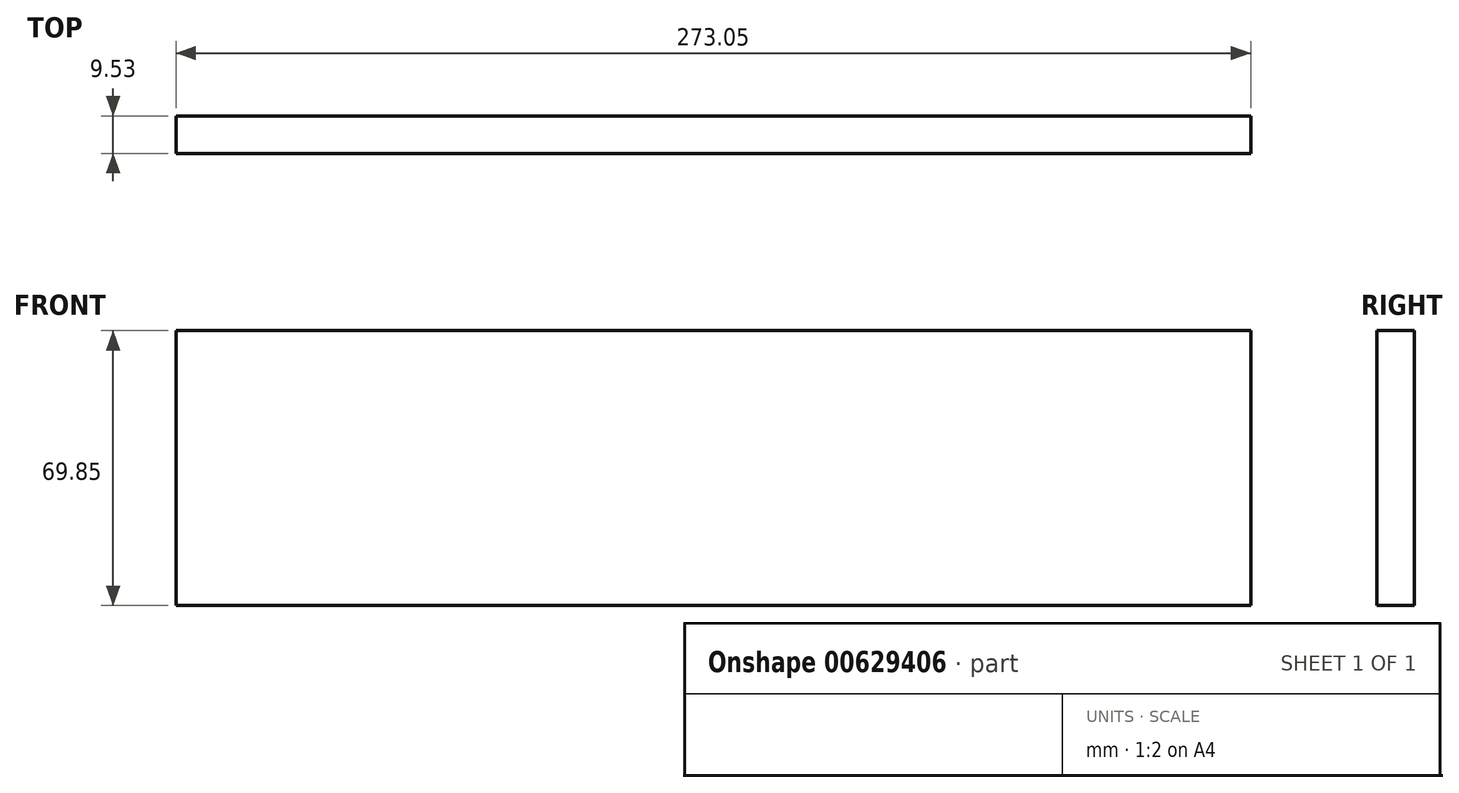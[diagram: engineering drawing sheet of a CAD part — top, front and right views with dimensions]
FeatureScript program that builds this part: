
annotation { "Feature Type Name" : "Feature", "Feature Type Description" : "" }
export const myFeature = defineFeature(function(context is Context, id is Id, definition is map)
    precondition{}
    {
        {
            var Q0;
            Q0=qCreatedBy(makeId("Front.planeOp"),FACE);
            var sketch = newSketch(context, id + "F0", { "sketchPlane" : qUnion([Q0])});
            skLineSegment(sketch, "E0.bottom", {"start": v(0, 0) * mm, "end": v(273.05, 0) * mm});
            skLineSegment(sketch, "E0.top", {"start": v(0, 69.85) * mm, "end": v(273.05, 69.85) * mm});
            skLineSegment(sketch, "E0.left", {"start": v(0, 0) * mm, "end": v(0, 69.85) * mm});
            skLineSegment(sketch, "E0.right", {"start": v(273.05, 0) * mm, "end": v(273.05, 69.85) * mm});
            skSolve(sketch);
        }
        {
            var Q0;
            Q0=qSketchRegion(id+"F0",true);
            extrude(context, id + "F1", {"entities" : qUnion([Q0]), "depth" : 9.52 * mm, "offsetDistance" : 25.4 * mm});
        }
    });
